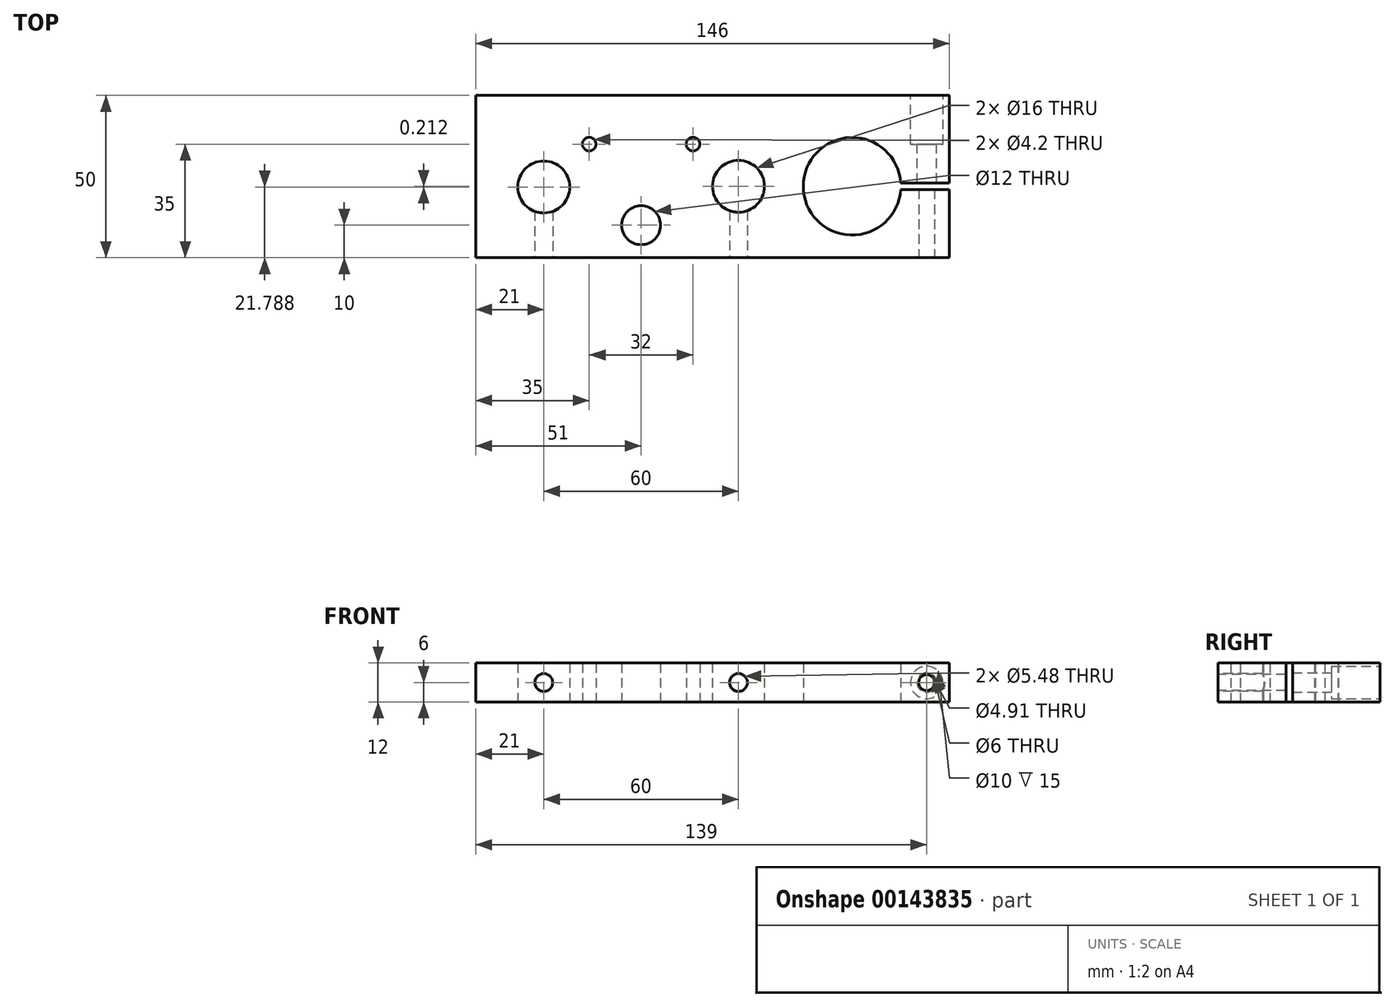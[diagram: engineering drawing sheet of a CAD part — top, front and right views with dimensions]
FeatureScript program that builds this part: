
annotation { "Feature Type Name" : "Feature", "Feature Type Description" : "" }
export const myFeature = defineFeature(function(context is Context, id is Id, definition is map)
    precondition{}
    {
        {
            var Q0;
            Q0=qCreatedBy(makeId("Top.planeOp"),FACE);
            var sketch = newSketch(context, id + "F0", { "sketchPlane" : qUnion([Q0])});
            skLineSegment(sketch, "E0.bottom", {"start": v(73, -25) * mm, "end": v(-73, -25) * mm});
            skLineSegment(sketch, "E0.top", {"start": v(73, 25) * mm, "end": v(-73, 25) * mm});
            skLineSegment(sketch, "E0.left", {"start": v(73, -25) * mm, "end": v(73, -4) * mm});
            skLineSegment(sketch, "E0.right", {"start": v(-73, -25) * mm, "end": v(-73, 25) * mm});
            skPoint(sketch, "E0.middle", {"position": v(0, 0) * mm});
            skLineSegment(sketch, "E1", {"start": v(58.05, -3) * mm, "end": v(-73, -3) * mm});
            skArc(sketch, "E2", {"start": v(58.02, -2) * mm, "mid": v(27.95, -3) * mm, "end": v(58.02, -4) * mm});
            skLineSegment(sketch, "E3", {"start": v(73, -2) * mm, "end": v(58.02, -2) * mm});
            skLineSegment(sketch, "E4", {"start": v(73, -4) * mm, "end": v(58.02, -4) * mm});
            skPoint(sketch, "E5.orphan", {"position": v(73, -3) * mm});
            skLineSegment(sketch, "E6.trimOffspring", {"start": v(73, -2) * mm, "end": v(73, 25) * mm});
            skCircle(sketch, "E7", {"center": v(8, -3) * mm, "radius": 8 * mm});
            skCircle(sketch, "E8", {"center": v(-52, -3.21) * mm, "radius": 8 * mm});
            skCircle(sketch, "E9", {"center": v(-22, -15) * mm, "radius": 6 * mm});
            skCircle(sketch, "E10", {"center": v(-6, 10) * mm, "radius": 2.1 * mm});
            skCircle(sketch, "E11", {"center": v(-38, 10) * mm, "radius": 2.1 * mm});
            skSolve(sketch);
        }
        {
            var Q0;
            {var subQ11=sQuery(id+"F0.wireOp",EDGE,"E0.top");Q0=makeQuery(id+"F0.imprint","IMPRINT",FACE,{"disambiguationData":[TD([[makeQuery(id+"F0.imprint","IMPRINT",EDGE,{"derivedFrom":subQ11}),1.0]])]});}
            var Q1;
            {var subQ12=sQuery(id+"F0.wireOp",EDGE,"E0.bottom");Q1=makeQuery(id+"F0.imprint","IMPRINT",FACE,{"disambiguationData":[TD([[makeQuery(id+"F0.imprint","IMPRINT",EDGE,{"derivedFrom":subQ12}),-1.0]])]});}
            extrude(context, id + "F1", {"entities" : qUnion([Q0, Q1]), "depth" : 12 * mm});
        }
        {
            var Q0;
            Q0=makeQuery(id+"F1.opExtrude","SWEPT_FACE",FACE,{"disambiguationData":[OSD([sQuery(id+"F0.wireOp",EDGE,"E0.bottom")])]});
            var sketch = newSketch(context, id + "F2", { "sketchPlane" : qUnion([Q0])});
            skCircle(sketch, "E12", {"center": v(66, 6) * mm, "radius": 2.5 * mm});
            skPoint(sketch, "E12.centerSnap0", {"position": v(73, 6) * mm});
            skSolve(sketch);
        }
        {
            var Q0;
            Q0=sQuery(id+"F2.wireOp",VERTEX,"E12.center");
            var Q1;
            Q1=makeQuery(id+"F1.opExtrude","SWEPT_BODY",BODY,{"disambiguationData":[OSD([sQuery(id+"F0.wireOp",EDGE,"E0.bottom"),sQuery(id+"F0.wireOp",EDGE,"E0.top"),sQuery(id+"F0.wireOp",EDGE,"E0.left"),sQuery(id+"F0.wireOp",EDGE,"E0.right"),sQuery(id+"F0.wireOp",EDGE,"E2"),sQuery(id+"F0.wireOp",EDGE,"E3"),sQuery(id+"F0.wireOp",EDGE,"E4"),sQuery(id+"F0.wireOp",EDGE,"E6.trimOffspring"),sQuery(id+"F0.wireOp",EDGE,"E7"),sQuery(id+"F0.wireOp",EDGE,"E8"),sQuery(id+"F0.wireOp",EDGE,"E9"),sQuery(id+"F0.wireOp",EDGE,"E10"),sQuery(id+"F0.wireOp",EDGE,"E11")])]});
            hole(context, id + "F3", {"style" : HoleStyle.SIMPLE, "endStyle" : HoleEndStyle.BLIND, "holeDiameter" : 4.9 * mm, "holeDepth" : 27 * mm, "startFromSketch" : true, "locations" : qUnion([Q0]), "scope" : qUnion([Q1])});
        }
        {
            var Q0;
            Q0=makeQuery(id+"F1.opExtrude","SWEPT_FACE",FACE,{"disambiguationData":[OSD([sQuery(id+"F0.wireOp",EDGE,"E0.top")])]});
            var sketch = newSketch(context, id + "F4", { "sketchPlane" : qUnion([Q0])});
            skCircle(sketch, "E13", {"center": v(-66, 6) * mm, "radius": 3.5 * mm});
            skSolve(sketch);
        }
        {
            var Q0;
            Q0=sQuery(id+"F4.wireOp",VERTEX,"E13.center");
            var Q1;
            Q1=makeQuery(id+"F1.opExtrude","SWEPT_BODY",BODY,{"disambiguationData":[OSD([sQuery(id+"F0.wireOp",EDGE,"E0.bottom"),sQuery(id+"F0.wireOp",EDGE,"E0.top"),sQuery(id+"F0.wireOp",EDGE,"E0.left"),sQuery(id+"F0.wireOp",EDGE,"E0.right"),sQuery(id+"F0.wireOp",EDGE,"E2"),sQuery(id+"F0.wireOp",EDGE,"E3"),sQuery(id+"F0.wireOp",EDGE,"E4"),sQuery(id+"F0.wireOp",EDGE,"E6.trimOffspring"),sQuery(id+"F0.wireOp",EDGE,"E7"),sQuery(id+"F0.wireOp",EDGE,"E8"),sQuery(id+"F0.wireOp",EDGE,"E9"),sQuery(id+"F0.wireOp",EDGE,"E10"),sQuery(id+"F0.wireOp",EDGE,"E11")])]});
            hole(context, id + "F5", {"style" : HoleStyle.C_BORE, "endStyle" : HoleEndStyle.BLIND, "holeDiameter" : 6 * mm, "cBoreDiameter" : 10 * mm, "cBoreDepth" : 15 * mm, "holeDepth" : 27 * mm, "startFromSketch" : true, "locations" : qUnion([Q0]), "scope" : qUnion([Q1])});
        }
        {
            var Q0;
            Q0=makeQuery(id+"F1.opExtrude","SWEPT_FACE",FACE,{"disambiguationData":[OSD([sQuery(id+"F0.wireOp",EDGE,"E0.bottom")])]});
            var sketch = newSketch(context, id + "F6", { "sketchPlane" : qUnion([Q0])});
            skCircle(sketch, "E14", {"center": v(-52, 6) * mm, "radius": 3.32 * mm});
            skCircle(sketch, "E15", {"center": v(8, 6) * mm, "radius": 3.3 * mm});
            skSolve(sketch);
        }
        {
            var Q0;
            Q0=sQuery(id+"F6.wireOp",VERTEX,"E14.center");
            var Q1;
            Q1=sQuery(id+"F6.wireOp",VERTEX,"E15.center");
            var Q2;
            Q2=makeQuery(id+"F1.opExtrude","SWEPT_BODY",BODY,{"disambiguationData":[OSD([sQuery(id+"F0.wireOp",EDGE,"E0.bottom"),sQuery(id+"F0.wireOp",EDGE,"E0.top"),sQuery(id+"F0.wireOp",EDGE,"E0.left"),sQuery(id+"F0.wireOp",EDGE,"E0.right"),sQuery(id+"F0.wireOp",EDGE,"E2"),sQuery(id+"F0.wireOp",EDGE,"E3"),sQuery(id+"F0.wireOp",EDGE,"E4"),sQuery(id+"F0.wireOp",EDGE,"E6.trimOffspring"),sQuery(id+"F0.wireOp",EDGE,"E7"),sQuery(id+"F0.wireOp",EDGE,"E8"),sQuery(id+"F0.wireOp",EDGE,"E9"),sQuery(id+"F0.wireOp",EDGE,"E10"),sQuery(id+"F0.wireOp",EDGE,"E11")])]});
            hole(context, id + "F7", {"style" : HoleStyle.SIMPLE, "endStyle" : HoleEndStyle.BLIND, "holeDiameter" : 5.48 * mm, "holeDepth" : 20 * mm, "startFromSketch" : true, "locations" : qUnion([Q0, Q1]), "scope" : qUnion([Q2])});
        }
    });
